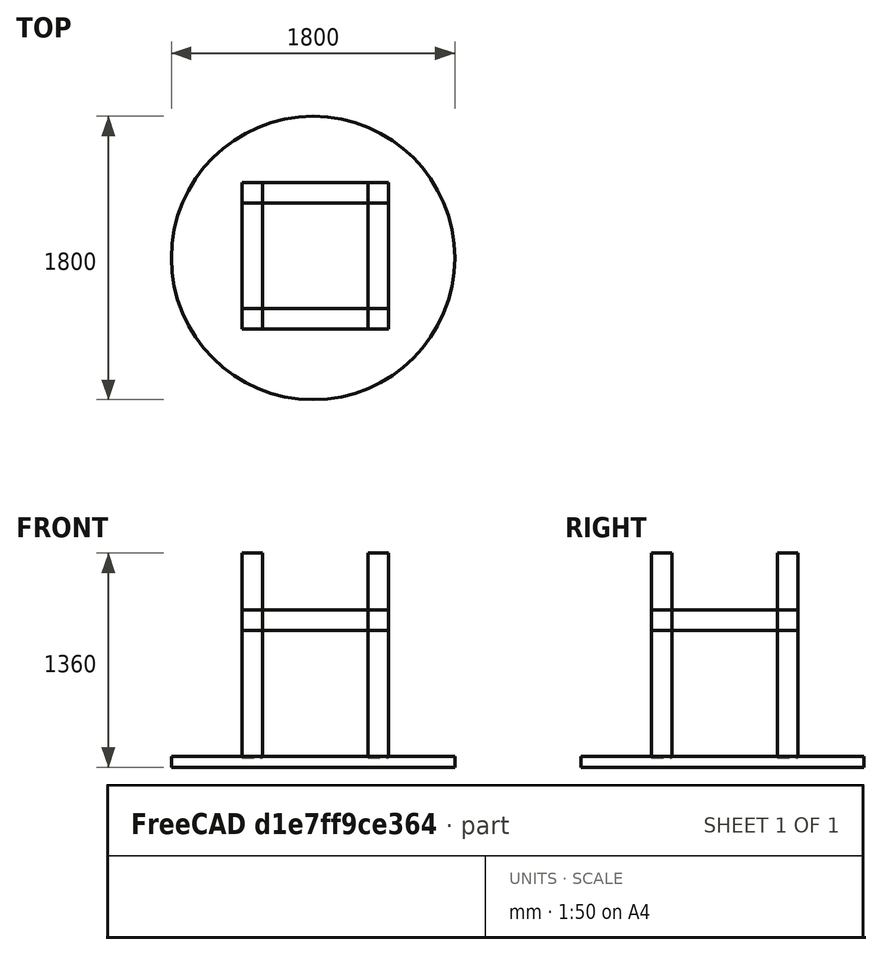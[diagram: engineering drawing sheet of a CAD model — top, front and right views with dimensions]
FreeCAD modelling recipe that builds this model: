
FCSTD DOCUMENT  (FreeCAD 1.0R38806 (Git))
Label: Mesa compleja
License: All rights reserved
LicenseURL: http://en.wikipedia.org/wiki/All_rights_reserved
objects: Part::Box×8, Part::Cylinder×1
note: 9 computed .brp shape members not serialized (recipe doc carries the construction recipe); baked Part::Feature solids carry a one-line shape summary decoded from their .brp

FEATURE [Part::Cylinder] Cylinder  label="Tablero"
  Angle = 360
  AttacherType = Attacher::AttachEngine3D
  FirstAngle = 0
  Height = 70
  Placement = pos=(-50,-50,0) rot=(0,0,1;0rad)
  Radius = 900
  SecondAngle = 0
FEATURE [Part::Box] Box  label="Pata1"
  AttacherType = Attacher::AttachEngine3D
  Height = 1300
  Length = 130
  Placement = pos=(-501,-500,60) rot=(0,0,1;0rad)
  Width = 130
FEATURE [Part::Box] Box001  label="Pata2"
  AttacherType = Attacher::AttachEngine3D
  Height = 1300
  Length = 130
  Placement = pos=(300,-500,60) rot=(0,0,1;0rad)
  Width = 130
FEATURE [Part::Box] Box002  label="Pata3"
  AttacherType = Attacher::AttachEngine3D
  Height = 1300
  Length = 130
  Placement = pos=(300,300,60) rot=(0,0,1;0rad)
  Width = 130
FEATURE [Part::Box] Box003  label="Pata4"
  AttacherType = Attacher::AttachEngine3D
  Height = 1300
  Length = 130
  Placement = pos=(-500,300,60) rot=(0,0,1;0rad)
  Width = 130
FEATURE [Part::Box] Box004  label="Union Pata1"
  AttacherType = Attacher::AttachEngine3D
  Height = 930
  Length = 130
  Placement = pos=(-500,300,1000) rot=(0,1,0;1.5708rad)
  Width = 130
FEATURE [Part::Box] Box005  label="Union Pata2"
  AttacherType = Attacher::AttachEngine3D
  Height = 930
  Length = 130
  Placement = pos=(-500,-500,1000) rot=(0,1,0;1.5708rad)
  Width = 130
FEATURE [Part::Box] Box006  label="Union Pata3"
  AttacherType = Attacher::AttachEngine3D
  Height = 930
  Length = 130
  Placement = pos=(-371,-500,870) rot=(0,1,1;3.14159rad)
  Width = 130
FEATURE [Part::Box] Box007  label="Union Pata4"
  AttacherType = Attacher::AttachEngine3D
  Height = 930
  Length = 130
  Placement = pos=(430,-500,870) rot=(0,1,1;3.14159rad)
  Width = 130
